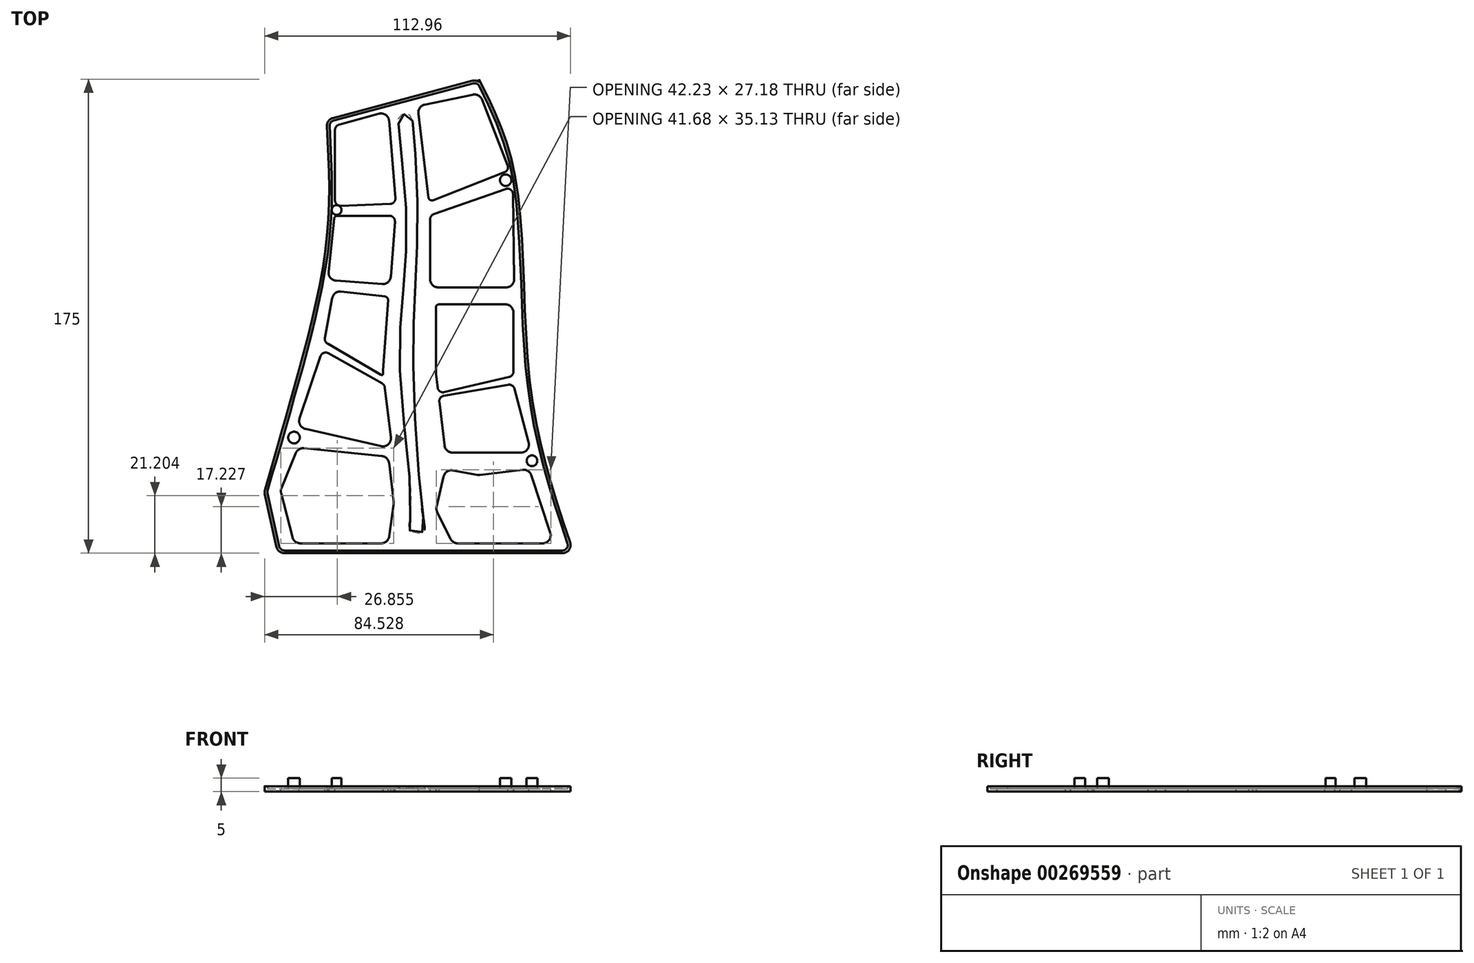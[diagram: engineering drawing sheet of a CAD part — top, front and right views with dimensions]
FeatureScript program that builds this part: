
annotation { "Feature Type Name" : "Feature", "Feature Type Description" : "" }
export const myFeature = defineFeature(function(context is Context, id is Id, definition is map)
    precondition{}
    {
        {
            var Q0;
            Q0=qCreatedBy(makeId("Top.planeOp"),FACE);
            var sketch = newSketch(context, id + "F0", { "sketchPlane" : qUnion([Q0])});
            skLineSegment(sketch, "E0", {"start": v(0, -62.14) * mm, "end": v(0, 112.86) * mm});
            skLineSegment(sketch, "E1", {"start": v(0, -62.14) * mm, "end": v(30.82, -62.14) * mm});
            skLineSegment(sketch, "E2", {"start": v(0, -62.14) * mm, "end": v(-74.2, -62.14) * mm});
            skLineSegment(sketch, "E3", {"start": v(-71.8, -62.14) * mm, "end": v(-49.49, -62.14) * mm});
            skLineSegment(sketch, "E4", {"start": v(-49.49, -62.14) * mm, "end": v(-49.49, 97.86) * mm});
            skLineSegment(sketch, "E5", {"start": v(-2.37, 112.23) * mm, "end": v(-53.92, 98.49) * mm});
            skFitSpline(sketch, "E6", {"points": [v(-80, -42.14) * mm, v(-67.91, 0) * mm, v(-56.29, 53.04) * mm, v(-56.29, 97.86) * mm], "startDerivative": vector(36.88, 126.58) * mm, "endDerivative": vector(-8, 134.66) * mm});
            skFitSpline(sketch, "E7", {"points": [v(0, 112.86) * mm, v(13.5, 76.24) * mm, v(18.95, 0) * mm, v(35, -62.14) * mm], "startDerivative": vector(59.17, -118.79) * mm, "endDerivative": vector(56.86, -167.73) * mm});
            skLineSegment(sketch, "E8", {"start": v(-79.06, -40.25) * mm, "end": v(-74.73, -59.8) * mm});
            skArc(sketch, "E9.filletArc", {"start": v(-53.92, 98.49) * mm, "mid": v(-55.58, 97.35) * mm, "end": v(-56.14, 95.41) * mm});
            skArc(sketch, "E10.filletArc", {"start": v(1.1, 110.66) * mm, "mid": v(-0.36, 112.06) * mm, "end": v(-2.37, 112.23) * mm});
            skArc(sketch, "E11.filletArc", {"start": v(30.82, -62.14) * mm, "mid": v(33.25, -60.9) * mm, "end": v(33.66, -58.18) * mm});
            skPoint(sketch, "E12.visualSharp", {"position": v(-74.2, -62.14) * mm});
            skArc(sketch, "E12.filletArc", {"start": v(-74.73, -59.8) * mm, "mid": v(-73.68, -61.48) * mm, "end": v(-71.8, -62.14) * mm});
            skPoint(sketch, "E13.visualSharp", {"position": v(-79.23, -39.5) * mm});
            skArc(sketch, "E13.filletArc", {"start": v(-79.02, -38.77) * mm, "mid": v(-79.13, -39.5) * mm, "end": v(-79.06, -40.25) * mm});
            skSolve(sketch);
        }
        {
            var Q0;
            Q0 = qSketchRegion(id + "F0", true);
            extrude(context, id + "F1", {"entities" : qUnion([Q0]), "depth" : 2 * mm});
        }
        {
            var Q0;
            Q0=makeQuery(id+"F1.opExtrude","CAP_FACE",FACE,{"disambiguationData":[OSD([sQuery(id+"F0.wireOp",EDGE,"E1"),sQuery(id+"F0.wireOp",EDGE,"E2"),sQuery(id+"F0.wireOp",EDGE,"E3"),sQuery(id+"F0.wireOp",EDGE,"E5"),sQuery(id+"F0.wireOp",EDGE,"E6"),sQuery(id+"F0.wireOp",EDGE,"E7"),sQuery(id+"F0.wireOp",EDGE,"E8")])],"isStart":false});
            shell(context, id + "F2", {"entities" : qUnion([Q0]), "thickness" : 1 * mm});
        }
        {
            var Q0;
            Q0=makeQuery(id+"F2.opShell","OFFSET_FACE",FACE,{"disambiguationData":[OSD([sQuery(id+"F0.wireOp",EDGE,"E1"),sQuery(id+"F0.wireOp",EDGE,"E2"),sQuery(id+"F0.wireOp",EDGE,"E3"),sQuery(id+"F0.wireOp",EDGE,"E5"),sQuery(id+"F0.wireOp",EDGE,"E6"),sQuery(id+"F0.wireOp",EDGE,"E7"),sQuery(id+"F0.wireOp",EDGE,"E8"),sQuery(id+"F0.wireOp",EDGE,"E9.filletArc"),sQuery(id+"F0.wireOp",EDGE,"E10.filletArc"),sQuery(id+"F0.wireOp",EDGE,"E11.filletArc"),sQuery(id+"F0.wireOp",EDGE,"E12.filletArc"),sQuery(id+"F0.wireOp",EDGE,"E13.filletArc")])]});
            var sketch = newSketch(context, id + "F3", { "sketchPlane" : qUnion([Q0])});
            skLineSegment(sketch, "E14", {"start": v(-36.97, 100.07) * mm, "end": v(-51.68, 96) * mm});
            skLineSegment(sketch, "E15", {"start": v(-53.15, 94.07) * mm, "end": v(-53.15, 68.1) * mm});
            skLineSegment(sketch, "E16", {"start": v(-53.5, 61.33) * mm, "end": v(-55.5, 41.75) * mm});
            skLineSegment(sketch, "E17", {"start": v(-52.74, 38.45) * mm, "end": v(-35.75, 37.2) * mm});
            skLineSegment(sketch, "E18", {"start": v(-32.53, 39.96) * mm, "end": v(-31.03, 60.26) * mm});
            skLineSegment(sketch, "E19", {"start": v(-30.85, 68.94) * mm, "end": v(-33.17, 97.43) * mm});
            skLineSegment(sketch, "E20", {"start": v(-22.37, 100.15) * mm, "end": v(-18.62, 69.13) * mm});
            skLineSegment(sketch, "E21", {"start": v(-18.02, 61.11) * mm, "end": v(-18.02, 38.97) * mm});
            skLineSegment(sketch, "E22", {"start": v(-15.02, 35.97) * mm, "end": v(10, 35.97) * mm});
            skLineSegment(sketch, "E23", {"start": v(13, 39.01) * mm, "end": v(12.55, 70.45) * mm});
            skLineSegment(sketch, "E24", {"start": v(10.6, 81.1) * mm, "end": v(1.12, 105.29) * mm});
            skLineSegment(sketch, "E25", {"start": v(-2.28, 107.13) * mm, "end": v(-20, 103.44) * mm});
            skLineSegment(sketch, "E26", {"start": v(-15.9, 28.5) * mm, "end": v(-15.9, 4.27) * mm});
            skLineSegment(sketch, "E27", {"start": v(-15.88, 3.91) * mm, "end": v(-15.28, -0.99) * mm});
            skLineSegment(sketch, "E28", {"start": v(-9.73, -25) * mm, "end": v(15.47, -25) * mm});
            skLineSegment(sketch, "E29", {"start": v(18.37, -21.24) * mm, "end": v(13.1, -1.4) * mm});
            skLineSegment(sketch, "E30", {"start": v(12.73, 4.9) * mm, "end": v(12.73, 26.71) * mm});
            skLineSegment(sketch, "E31", {"start": v(9.73, 29.71) * mm, "end": v(-13.49, 29.71) * mm});
            skLineSegment(sketch, "E32", {"start": v(-13.49, 29.71) * mm, "end": v(-14.7, 29.71) * mm});
            skLineSegment(sketch, "E33", {"start": v(-33.55, 31.31) * mm, "end": v(-35.45, 5.31) * mm});
            skLineSegment(sketch, "E34", {"start": v(-35.44, 4.93) * mm, "end": v(-35.35, 4.2) * mm});
            skLineSegment(sketch, "E35", {"start": v(-36.16, -22.64) * mm, "end": v(-64.04, -16.27) * mm});
            skLineSegment(sketch, "E36", {"start": v(-66.21, -12.39) * mm, "end": v(-58.5, 10.57) * mm});
            skLineSegment(sketch, "E37", {"start": v(-56.88, 17.3) * mm, "end": v(-54.17, 32) * mm});
            skLineSegment(sketch, "E38", {"start": v(-50.88, 34.44) * mm, "end": v(-34.62, 32.6) * mm});
            skLineSegment(sketch, "E39", {"start": v(-33.18, -28.89) * mm, "end": v(-31.47, -43.1) * mm});
            skLineSegment(sketch, "E40", {"start": v(-31.47, -43.87) * mm, "end": v(-33.12, -55.9) * mm});
            skLineSegment(sketch, "E41", {"start": v(-36.09, -58.5) * mm, "end": v(-65.93, -58.5) * mm});
            skLineSegment(sketch, "E42", {"start": v(-68.84, -56.25) * mm, "end": v(-73.03, -40) * mm});
            skLineSegment(sketch, "E43", {"start": v(-72.9, -38.13) * mm, "end": v(-67.67, -25.23) * mm});
            skLineSegment(sketch, "E44", {"start": v(-64.59, -23.38) * mm, "end": v(-35.86, -26.26) * mm});
            skLineSegment(sketch, "E45", {"start": v(-13.04, -33.82) * mm, "end": v(-15.65, -44.83) * mm});
            skLineSegment(sketch, "E46", {"start": v(-15.42, -46.85) * mm, "end": v(-10.48, -56.83) * mm});
            skLineSegment(sketch, "E47", {"start": v(-7.79, -58.5) * mm, "end": v(23.51, -58.5) * mm});
            skLineSegment(sketch, "E48", {"start": v(26.36, -54.56) * mm, "end": v(19.35, -33.38) * mm});
            skLineSegment(sketch, "E49", {"start": v(16.14, -31.34) * mm, "end": v(0.45, -33.24) * mm});
            skLineSegment(sketch, "E50", {"start": v(-0.44, -33.2) * mm, "end": v(-9.59, -31.55) * mm});
            skPoint(sketch, "E51.visualSharp", {"position": v(-12.39, -31.05) * mm});
            skArc(sketch, "E51.filletArc", {"start": v(-9.59, -31.55) * mm, "mid": v(-11.76, -32) * mm, "end": v(-13.04, -33.82) * mm});
            skPoint(sketch, "E52.visualSharp", {"position": v(0, -33.3) * mm});
            skArc(sketch, "E52.filletArc", {"start": v(-0.44, -33.2) * mm, "mid": v(0, -33.26) * mm, "end": v(0.45, -33.24) * mm});
            skPoint(sketch, "E53.visualSharp", {"position": v(18.58, -31.05) * mm});
            skArc(sketch, "E53.filletArc", {"start": v(19.35, -33.38) * mm, "mid": v(18.1, -31.79) * mm, "end": v(16.14, -31.34) * mm});
            skPoint(sketch, "E54.visualSharp", {"position": v(27.67, -58.5) * mm});
            skArc(sketch, "E54.filletArc", {"start": v(23.51, -58.5) * mm, "mid": v(25.95, -57.26) * mm, "end": v(26.36, -54.56) * mm});
            skPoint(sketch, "E55.visualSharp", {"position": v(-9.65, -58.5) * mm});
            skArc(sketch, "E55.filletArc", {"start": v(-10.48, -56.83) * mm, "mid": v(-9.37, -58.05) * mm, "end": v(-7.79, -58.5) * mm});
            skPoint(sketch, "E56.visualSharp", {"position": v(-15.9, -45.88) * mm});
            skArc(sketch, "E56.filletArc", {"start": v(-15.65, -44.83) * mm, "mid": v(-15.7, -45.86) * mm, "end": v(-15.42, -46.85) * mm});
            skPoint(sketch, "E57.visualSharp", {"position": v(-31.42, -43.49) * mm});
            skArc(sketch, "E57.filletArc", {"start": v(-31.47, -43.87) * mm, "mid": v(-31.44, -43.49) * mm, "end": v(-31.47, -43.1) * mm});
            skPoint(sketch, "E58.visualSharp", {"position": v(-33.47, -26.5) * mm});
            skArc(sketch, "E58.filletArc", {"start": v(-33.18, -28.89) * mm, "mid": v(-34.06, -27.1) * mm, "end": v(-35.86, -26.26) * mm});
            skPoint(sketch, "E59.visualSharp", {"position": v(-66.82, -23.15) * mm});
            skArc(sketch, "E59.filletArc", {"start": v(-64.59, -23.38) * mm, "mid": v(-66.43, -23.8) * mm, "end": v(-67.67, -25.23) * mm});
            skPoint(sketch, "E60.visualSharp", {"position": v(-73.28, -39.04) * mm});
            skArc(sketch, "E60.filletArc", {"start": v(-72.9, -38.13) * mm, "mid": v(-73.12, -39.06) * mm, "end": v(-73.03, -40) * mm});
            skPoint(sketch, "E61.visualSharp", {"position": v(-68.26, -58.5) * mm});
            skArc(sketch, "E61.filletArc", {"start": v(-68.84, -56.25) * mm, "mid": v(-67.77, -57.87) * mm, "end": v(-65.93, -58.5) * mm});
            skPoint(sketch, "E62.visualSharp", {"position": v(-33.47, -58.5) * mm});
            skArc(sketch, "E62.filletArc", {"start": v(-36.09, -58.5) * mm, "mid": v(-34.12, -57.76) * mm, "end": v(-33.12, -55.9) * mm});
            skPoint(sketch, "E63.visualSharp", {"position": v(-32, -23.6) * mm});
            skArc(sketch, "E63.filletArc", {"start": v(-36.16, -22.64) * mm, "mid": v(-33.48, -21.95) * mm, "end": v(-32.51, -19.36) * mm});
            skPoint(sketch, "E64.visualSharp", {"position": v(-67.27, -15.53) * mm});
            skArc(sketch, "E64.filletArc", {"start": v(-66.21, -12.39) * mm, "mid": v(-65.99, -14.8) * mm, "end": v(-64.04, -16.27) * mm});
            skPoint(sketch, "E65.visualSharp", {"position": v(-12.39, -25) * mm});
            skArc(sketch, "E65.filletArc", {"start": v(-12.7, -22.37) * mm, "mid": v(-11.72, -24.25) * mm, "end": v(-9.73, -25) * mm});
            skPoint(sketch, "E66.visualSharp", {"position": v(19.36, -25) * mm});
            skArc(sketch, "E66.filletArc", {"start": v(15.47, -25) * mm, "mid": v(17.84, -23.84) * mm, "end": v(18.37, -21.24) * mm});
            skPoint(sketch, "E67.visualSharp", {"position": v(12.73, 29.71) * mm});
            skArc(sketch, "E67.filletArc", {"start": v(12.73, 26.71) * mm, "mid": v(11.86, 28.83) * mm, "end": v(9.73, 29.71) * mm});
            skPoint(sketch, "E68.visualSharp", {"position": v(12.73, 0) * mm});
            skArc(sketch, "E68.filletArc", {"start": v(12.73, 0.4) * mm, "mid": v(12.76, 0) * mm, "end": v(12.83, -0.38) * mm});
            skPoint(sketch, "E69.visualSharp", {"position": v(-15.9, 4.1) * mm});
            skArc(sketch, "E69.filletArc", {"start": v(-15.9, 4.27) * mm, "mid": v(-15.9, 4.1) * mm, "end": v(-15.88, 3.91) * mm});
            skPoint(sketch, "E70.visualSharp", {"position": v(-15.9, 29.71) * mm});
            skArc(sketch, "E70.filletArc", {"start": v(-14.7, 29.71) * mm, "mid": v(-15.54, 29.36) * mm, "end": v(-15.9, 28.5) * mm});
            skPoint(sketch, "E71.visualSharp", {"position": v(-33.47, 32.47) * mm});
            skArc(sketch, "E71.filletArc", {"start": v(-33.55, 31.31) * mm, "mid": v(-33.83, 32.17) * mm, "end": v(-34.62, 32.6) * mm});
            skPoint(sketch, "E72.visualSharp", {"position": v(-53.66, 34.76) * mm});
            skArc(sketch, "E72.filletArc", {"start": v(-50.88, 34.44) * mm, "mid": v(-53, 33.87) * mm, "end": v(-54.17, 32) * mm});
            skPoint(sketch, "E73.visualSharp", {"position": v(-35.47, 5.12) * mm});
            skArc(sketch, "E73.filletArc", {"start": v(-35.45, 5.31) * mm, "mid": v(-35.46, 5.12) * mm, "end": v(-35.44, 4.93) * mm});
            skPoint(sketch, "E74.visualSharp", {"position": v(-57.66, 13.06) * mm});
            skArc(sketch, "E74.filletArc", {"start": v(-57.73, 12.86) * mm, "mid": v(-57.67, 13.06) * mm, "end": v(-57.62, 13.27) * mm});
            skPoint(sketch, "E75.visualSharp", {"position": v(-18.02, 35.97) * mm});
            skArc(sketch, "E75.filletArc", {"start": v(-18.02, 38.97) * mm, "mid": v(-17.15, 36.85) * mm, "end": v(-15.02, 35.97) * mm});
            skPoint(sketch, "E76.visualSharp", {"position": v(13.04, 35.97) * mm});
            skArc(sketch, "E76.filletArc", {"start": v(10, 35.97) * mm, "mid": v(12.13, 36.86) * mm, "end": v(13, 39.01) * mm});
            skPoint(sketch, "E77.visualSharp", {"position": v(0.2, 107.65) * mm});
            skArc(sketch, "E77.filletArc", {"start": v(1.12, 105.29) * mm, "mid": v(-0.24, 106.83) * mm, "end": v(-2.28, 107.13) * mm});
            skPoint(sketch, "E78.visualSharp", {"position": v(-22.7, 102.88) * mm});
            skArc(sketch, "E78.filletArc", {"start": v(-20, 103.44) * mm, "mid": v(-21.83, 102.25) * mm, "end": v(-22.37, 100.15) * mm});
            skPoint(sketch, "E79.visualSharp", {"position": v(12.47, 76.3) * mm});
            skArc(sketch, "E79.filletArc", {"start": v(12.48, 75.4) * mm, "mid": v(12.39, 76.3) * mm, "end": v(12.14, 77.15) * mm});
            skPoint(sketch, "E80.visualSharp", {"position": v(-18.02, 64.16) * mm});
            skArc(sketch, "E80.filletArc", {"start": v(-18.02, 64.09) * mm, "mid": v(-18.03, 64.16) * mm, "end": v(-18.03, 64.23) * mm});
            skPoint(sketch, "E81.visualSharp", {"position": v(-30.6, 65.93) * mm});
            skArc(sketch, "E81.filletArc", {"start": v(-30.61, 65.84) * mm, "mid": v(-30.61, 65.93) * mm, "end": v(-30.62, 66.03) * mm});
            skPoint(sketch, "E82.visualSharp", {"position": v(-53.15, 64.81) * mm});
            skArc(sketch, "E82.filletArc", {"start": v(-53.15, 64.75) * mm, "mid": v(-53.15, 64.81) * mm, "end": v(-53.15, 64.87) * mm});
            skPoint(sketch, "E83.visualSharp", {"position": v(-32.75, 36.97) * mm});
            skArc(sketch, "E83.filletArc", {"start": v(-35.75, 37.2) * mm, "mid": v(-33.56, 37.91) * mm, "end": v(-32.53, 39.96) * mm});
            skPoint(sketch, "E84.visualSharp", {"position": v(-55.82, 38.68) * mm});
            skArc(sketch, "E84.filletArc", {"start": v(-55.5, 41.75) * mm, "mid": v(-54.82, 39.52) * mm, "end": v(-52.74, 38.45) * mm});
            skPoint(sketch, "E85.visualSharp", {"position": v(-33.47, 101.04) * mm});
            skArc(sketch, "E85.filletArc", {"start": v(-33.17, 97.43) * mm, "mid": v(-34.45, 99.64) * mm, "end": v(-36.97, 100.07) * mm});
            skPoint(sketch, "E86.visualSharp", {"position": v(-53.15, 95.59) * mm});
            skArc(sketch, "E86.filletArc", {"start": v(-51.68, 96) * mm, "mid": v(-52.74, 95.28) * mm, "end": v(-53.15, 94.07) * mm});
            skLineSegment(sketch, "E87", {"start": v(-16.99, 68.15) * mm, "end": v(9.46, 78.5) * mm});
            skLineSegment(sketch, "E88", {"start": v(9.89, 72.3) * mm, "end": v(-16.68, 63) * mm});
            skLineSegment(sketch, "E89", {"start": v(-33.02, 62.41) * mm, "end": v(-52.3, 62.41) * mm});
            skLineSegment(sketch, "E90", {"start": v(-32.77, 66.78) * mm, "end": v(-51.07, 66.1) * mm});
            skPoint(sketch, "E91.visualSharp", {"position": v(-18.44, 67.59) * mm});
            skArc(sketch, "E91.filletArc", {"start": v(-18.62, 69.13) * mm, "mid": v(-18.05, 68.24) * mm, "end": v(-16.99, 68.15) * mm});
            skPoint(sketch, "E92.visualSharp", {"position": v(11.32, 79.24) * mm});
            skArc(sketch, "E92.filletArc", {"start": v(9.46, 78.5) * mm, "mid": v(10.56, 79.57) * mm, "end": v(10.6, 81.1) * mm});
            skPoint(sketch, "E93.visualSharp", {"position": v(12.5, 73.23) * mm});
            skArc(sketch, "E93.filletArc", {"start": v(12.55, 70.45) * mm, "mid": v(11.7, 72.06) * mm, "end": v(9.89, 72.3) * mm});
            skPoint(sketch, "E94.visualSharp", {"position": v(-18.02, 62.53) * mm});
            skArc(sketch, "E94.filletArc", {"start": v(-16.68, 63) * mm, "mid": v(-17.66, 62.27) * mm, "end": v(-18.02, 61.11) * mm});
            skPoint(sketch, "E95.visualSharp", {"position": v(-30.87, 62.41) * mm});
            skArc(sketch, "E95.filletArc", {"start": v(-31.03, 60.26) * mm, "mid": v(-31.56, 61.77) * mm, "end": v(-33.02, 62.41) * mm});
            skPoint(sketch, "E96.visualSharp", {"position": v(-53.4, 62.41) * mm});
            skArc(sketch, "E96.filletArc", {"start": v(-52.3, 62.41) * mm, "mid": v(-53.11, 62.1) * mm, "end": v(-53.5, 61.33) * mm});
            skPoint(sketch, "E97.visualSharp", {"position": v(-53.15, 66.03) * mm});
            skArc(sketch, "E97.filletArc", {"start": v(-53.15, 68.1) * mm, "mid": v(-52.53, 66.67) * mm, "end": v(-51.07, 66.1) * mm});
            skPoint(sketch, "E98.visualSharp", {"position": v(-30.68, 66.85) * mm});
            skArc(sketch, "E98.filletArc", {"start": v(-32.77, 66.78) * mm, "mid": v(-31.35, 67.45) * mm, "end": v(-30.85, 68.94) * mm});
            skLineSegment(sketch, "E99", {"start": v(-13, -4.04) * mm, "end": v(10.83, 0.06) * mm});
            skLineSegment(sketch, "E100", {"start": v(11.2, 2.96) * mm, "end": v(-12.84, -2.7) * mm});
            skLineSegment(sketch, "E101", {"start": v(-35.73, 0.5) * mm, "end": v(-55.62, 11.67) * mm});
            skLineSegment(sketch, "E102", {"start": v(-55.92, 15.2) * mm, "end": v(-36.12, 3.7) * mm});
            skLineSegment(sketch, "E103.trimOffspring", {"start": v(-14.65, -6.25) * mm, "end": v(-12.7, -22.37) * mm});
            skLineSegment(sketch, "E104.trimOffspring", {"start": v(-34.73, -1) * mm, "end": v(-32.51, -19.36) * mm});
            skPoint(sketch, "E105.visualSharp", {"position": v(-15.02, -3.2) * mm});
            skArc(sketch, "E105.filletArc", {"start": v(-15.28, -0.99) * mm, "mid": v(-14.44, -2.39) * mm, "end": v(-12.84, -2.7) * mm});
            skPoint(sketch, "E106.visualSharp", {"position": v(12.73, 3.32) * mm});
            skArc(sketch, "E106.filletArc", {"start": v(11.2, 2.96) * mm, "mid": v(12.3, 3.66) * mm, "end": v(12.73, 4.9) * mm});
            skArc(sketch, "E107.filletArc", {"start": v(13.1, -1.4) * mm, "mid": v(12.25, -0.22) * mm, "end": v(10.83, 0.06) * mm});
            skPoint(sketch, "E108.visualSharp", {"position": v(-14.88, -4.36) * mm});
            skArc(sketch, "E108.filletArc", {"start": v(-13, -4.04) * mm, "mid": v(-14.27, -4.82) * mm, "end": v(-14.65, -6.25) * mm});
            skPoint(sketch, "E109.visualSharp", {"position": v(-34.85, 0) * mm});
            skArc(sketch, "E109.filletArc", {"start": v(-34.73, -1) * mm, "mid": v(-35.05, -0.13) * mm, "end": v(-35.73, 0.5) * mm});
            skPoint(sketch, "E110.visualSharp", {"position": v(-35.23, 3.19) * mm});
            skArc(sketch, "E110.filletArc", {"start": v(-36.12, 3.7) * mm, "mid": v(-35.58, 3.72) * mm, "end": v(-35.35, 4.2) * mm});
            skPoint(sketch, "E111.visualSharp", {"position": v(-57.73, 12.86) * mm});
            skArc(sketch, "E111.filletArc", {"start": v(-55.62, 11.67) * mm, "mid": v(-57.32, 11.8) * mm, "end": v(-58.5, 10.57) * mm});
            skPoint(sketch, "E112.visualSharp", {"position": v(-57.14, 15.9) * mm});
            skArc(sketch, "E112.filletArc", {"start": v(-56.88, 17.3) * mm, "mid": v(-56.73, 16.1) * mm, "end": v(-55.92, 15.2) * mm});
            skSolve(sketch);
        }
        {
            var Q0;
            Q0 = qSketchRegion(id + "F3", true);
            extrude(context, id + "F4", {"entities" : qUnion([Q0]), "operationType" : NewBodyOperationType.REMOVE, "oppositeDirection" : true, "depth" : 25 * mm});
        }
        {
            var Q0;
            Q0=makeQuery(id+"F2.opShell","OFFSET_FACE",FACE,{"disambiguationData":[OSD([sQuery(id+"F0.wireOp",EDGE,"E1"),sQuery(id+"F0.wireOp",EDGE,"E2"),sQuery(id+"F0.wireOp",EDGE,"E3"),sQuery(id+"F0.wireOp",EDGE,"E5"),sQuery(id+"F0.wireOp",EDGE,"E6"),sQuery(id+"F0.wireOp",EDGE,"E7"),sQuery(id+"F0.wireOp",EDGE,"E8"),sQuery(id+"F0.wireOp",EDGE,"E9.filletArc"),sQuery(id+"F0.wireOp",EDGE,"E10.filletArc"),sQuery(id+"F0.wireOp",EDGE,"E11.filletArc"),sQuery(id+"F0.wireOp",EDGE,"E12.filletArc"),sQuery(id+"F0.wireOp",EDGE,"E13.filletArc")])]});
            var sketch = newSketch(context, id + "F5", { "sketchPlane" : qUnion([Q0])});
            skPoint(sketch, "E113.1.internal.snap0", {"position": v(-34.45, 99.64) * mm});
            skPoint(sketch, "E113.2.internal.snap0", {"position": v(-34.45, 99.64) * mm});
            skPoint(sketch, "E113.10.internal.snap0", {"position": v(-20.5, -61.14) * mm});
            skPoint(sketch, "E113.11.internal.snap0", {"position": v(-20.5, -61.14) * mm});
            skFitSpline(sketch, "E113", {"points": [v(-24.46, 97.43) * mm, v(-25.6, 99.64) * mm, v(-29.01, 99.64) * mm, v(-29.77, 97.43) * mm, v(-26.93, 65.36) * mm, v(-28.07, 33.65) * mm, v(-28.94, 0) * mm, v(-25.18, -46.56) * mm, v(-25.93, -53.1) * mm, v(-23.84, -54.62) * mm, v(-20.5, -54.05) * mm, v(-20.5, -49.5) * mm, v(-24.03, -1.84) * mm, v(-23.7, 33.36) * mm, v(-22.7, 65.84) * mm, v(-24.46, 97.43) * mm]});
            skSolve(sketch);
        }
        {
            var Q0;
            Q0 = qSketchRegion(id + "F5", true);
            extrude(context, id + "F6", {"entities" : qUnion([Q0]), "operationType" : NewBodyOperationType.ADD, "depth" : 1 * mm});
        }
        {
            var Q0;
            Q0=makeQuery(id+"F2.opShell","OFFSET_FACE",FACE,{"disambiguationData":[OSD([sQuery(id+"F0.wireOp",EDGE,"E1"),sQuery(id+"F0.wireOp",EDGE,"E2"),sQuery(id+"F0.wireOp",EDGE,"E3"),sQuery(id+"F0.wireOp",EDGE,"E5"),sQuery(id+"F0.wireOp",EDGE,"E6"),sQuery(id+"F0.wireOp",EDGE,"E7"),sQuery(id+"F0.wireOp",EDGE,"E8"),sQuery(id+"F0.wireOp",EDGE,"E9.filletArc"),sQuery(id+"F0.wireOp",EDGE,"E10.filletArc"),sQuery(id+"F0.wireOp",EDGE,"E11.filletArc"),sQuery(id+"F0.wireOp",EDGE,"E12.filletArc"),sQuery(id+"F0.wireOp",EDGE,"E13.filletArc")])]});
            var sketch = newSketch(context, id + "F7", { "sketchPlane" : qUnion([Q0])});
            skCircle(sketch, "E114", {"center": v(-52.53, 64.56) * mm, "radius": 1.8 * mm});
            skPoint(sketch, "E114.centerSnap0", {"position": v(-52.53, 66.67) * mm});
            skCircle(sketch, "E115", {"center": v(-68.28, -19.46) * mm, "radius": 2.16 * mm});
            skCircle(sketch, "E116", {"center": v(19.58, -28.01) * mm, "radius": 1.98 * mm});
            skCircle(sketch, "E117", {"center": v(9.89, 75.55) * mm, "radius": 2.12 * mm});
            skSolve(sketch);
        }
        {
            var Q0;
            Q0 = qSketchRegion(id + "F7", true);
            extrude(context, id + "F8", {"entities" : qUnion([Q0]), "operationType" : NewBodyOperationType.ADD, "depth" : 4 * mm});
        }
    });
